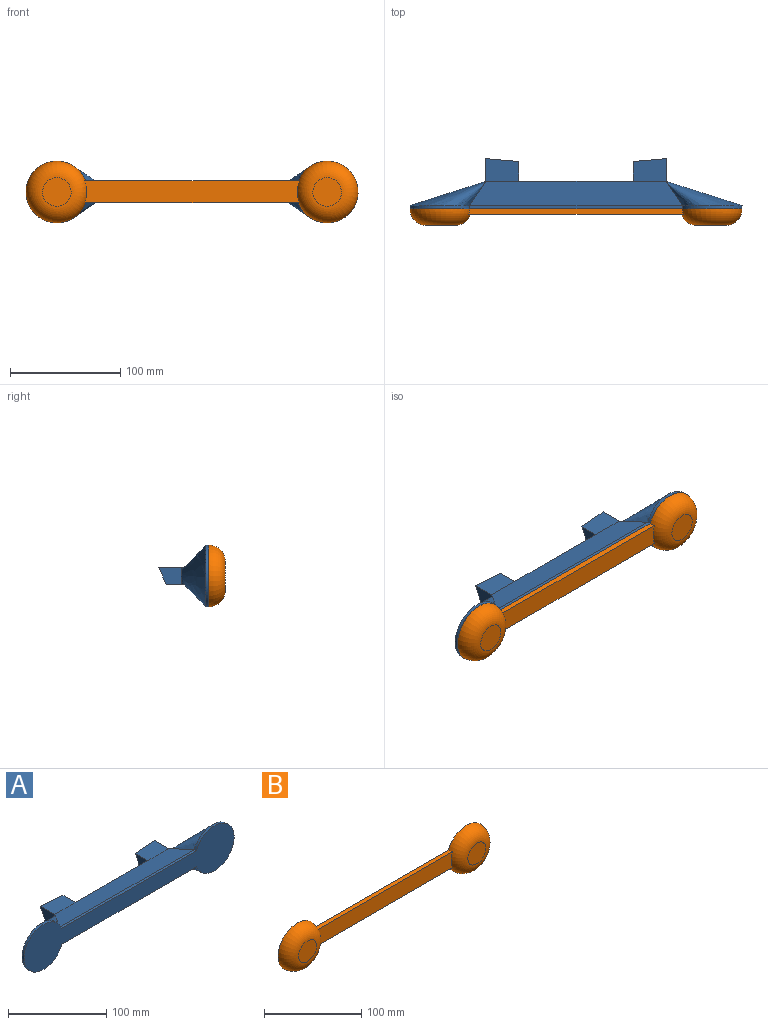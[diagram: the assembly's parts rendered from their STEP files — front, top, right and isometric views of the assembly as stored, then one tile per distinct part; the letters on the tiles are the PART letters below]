
ASSEMBLY  parts=2 mates=1
PART A: 35 faces, bbox 301.8x45.6x56 mm
  f0: plane 11.15x2mm, normal (0,0,-1), area 22.1mm2, adj f9,f16,f18,f30
  f1: plane 11.15x2mm, normal (0,0,-1), area 22.1mm2, adj f9,f22,f27,f33
  f2: plane 26x13mm, normal (0,1,0), area 338mm2, adj f9,f22,f23,f24
  f3: plane 104x15mm, normal (0,1,0), area 1560mm2, adj f9,f11,f18,f27
  f4: plane 193.52x3mm, normal (0,0,1), area 580.6mm2, adj f5,f7,f8,f11
  f5: cylinder r=28mm len=56mm, axis (0,-1,0), area 466.4mm2, adj f4,f6,f8,f10
  f6: plane 193.52x3mm, normal (0,0,-1), area 580.6mm2, adj f5,f7,f8,f9
  f7: cylinder r=28mm len=56mm, axis (0,-1,0), area 466.4mm2, adj f4,f6,f8,f12
  f8: plane 301.83x56mm, normal (0,-1,0), area 8746.8mm2, adj f4,f5,f6,f7
  f9: plane 193.52x22mm, normal (0,0.11,-0.99), area 3958mm2, adj f0,f1,f2,f3,f6,f10,f12,f13
  f10: bspline ~68.91x56.03mm, area 3599.2mm2, adj f5,f9,f11,f20
  f11: plane 193.52x22mm, normal (0,0.11,0.99), area 3958mm2, adj f3,f4,f10,f12,f19,f26
  f12: bspline ~68.91x56.03mm, area 3599.2mm2, adj f7,f9,f11,f25
  f13: plane 26x13mm, normal (0,1,0), area 338mm2, adj f9,f14,f15,f16
  f14: plane 15x13mm, normal (1,0,0), area 192.4mm2, adj f13,f15,f17,f28,f30
  f15: plane 26x15mm, normal (0,0,-1), area 390mm2, adj f13,f14,f16,f28
  f16: plane 15x13mm, normal (-1,0,0), area 179.2mm2, adj f0,f13,f15,f28,f30
  f17: plane 13.6x2mm, normal (0,0,-1), area 27mm2, adj f9,f14,f20,f30
  f18: plane 18x15mm, normal (1,0,0), area 217.3mm2, adj f0,f3,f19,f30
  f19: plane 30x20.62mm, normal (0,0,1), area 579.4mm2, adj f11,f18,f20,f30
  f20: plane 20.62x15mm, normal (-1,0,0), area 256.7mm2, adj f10,f17,f19,f30
  f21: plane 13.6x2mm, normal (0,0,-1), area 27mm2, adj f9,f24,f25,f33
  f22: plane 15x13mm, normal (1,0,0), area 179.2mm2, adj f1,f2,f23,f33,f34
  f23: plane 26x15mm, normal (0,0,-1), area 390mm2, adj f2,f22,f24,f34
  f24: plane 15x13mm, normal (-1,0,0), area 192.4mm2, adj f2,f21,f23,f33,f34
  f25: plane 20.62x15mm, normal (1,0,0), area 256.7mm2, adj f12,f21,f26,f33
  f26: plane 30x20.62mm, normal (0,0,1), area 579.4mm2, adj f11,f25,f27,f33
  f27: plane 18x15mm, normal (-1,0,0), area 217.3mm2, adj f1,f3,f26,f33
  f28: plane 26x9.64mm, normal (0,-1,0), area 169.2mm2, adj f14,f15,f16,f29,f30
  f29: cylinder r=3mm len=6mm, axis (0,-1,0), area 12mm2, adj f28,f30
  f30: plane 30x15mm, normal (0.08,0.9,-0.42), area 311.5mm2, adj f0,f14,f16,f17,f18,f19,f20,f28
  f31: cylinder r=3mm len=6mm, axis (0,-1,0), area 18.3mm2, adj f33,f34
  f32: cylinder r=3mm len=5.85mm, axis (0,-1,0), area 6.8mm2, adj f33,f34
  f33: plane 30x15mm, normal (-0.08,0.9,-0.42), area 291.9mm2, adj f1,f21,f22,f24,f25,f26,f27,f31
  f34: plane 26x9.64mm, normal (0,-1,0), area 151.5mm2, adj f22,f23,f24,f31,f32,f33
PART B: 8 faces, bbox 301.8x15x56 mm
  f0: plane 195.36x5mm, normal (0,0,1), area 970.6mm2, adj f2,f3,f6,f7
  f1: plane 195.36x5mm, normal (0,0,-1), area 970.6mm2, adj f2,f3,f6,f7
  f2: plane 195.36x20mm, normal (0,-1,0), area 3855.9mm2, adj f0,f1,f6,f7
  f3: plane 301.83x56mm, normal (0,1,0), area 8746.8mm2, adj f0,f1,f6,f7
  f4: plane 26x26mm, normal (0,-1,0), area 530.9mm2, adj f7
  f5: plane 26x26mm, normal (0,-1,0), area 530.9mm2, adj f6
  f6: torus R=13mm, axis (0,-1,0), area 3234mm2, adj f0,f1,f2,f3,f5
  f7: torus R=13mm, axis (0,-1,0), area 3234mm2, adj f0,f1,f2,f3,f4
PLACE A t=(146.9,-68.61,43.89)mm
PLACE B t=(146.9,-68.61,43.89)mm
MATE fastened A.f8 <-> B.f3  axis (0,-1,0) through (-159.84,-68.61,43.89)mm
